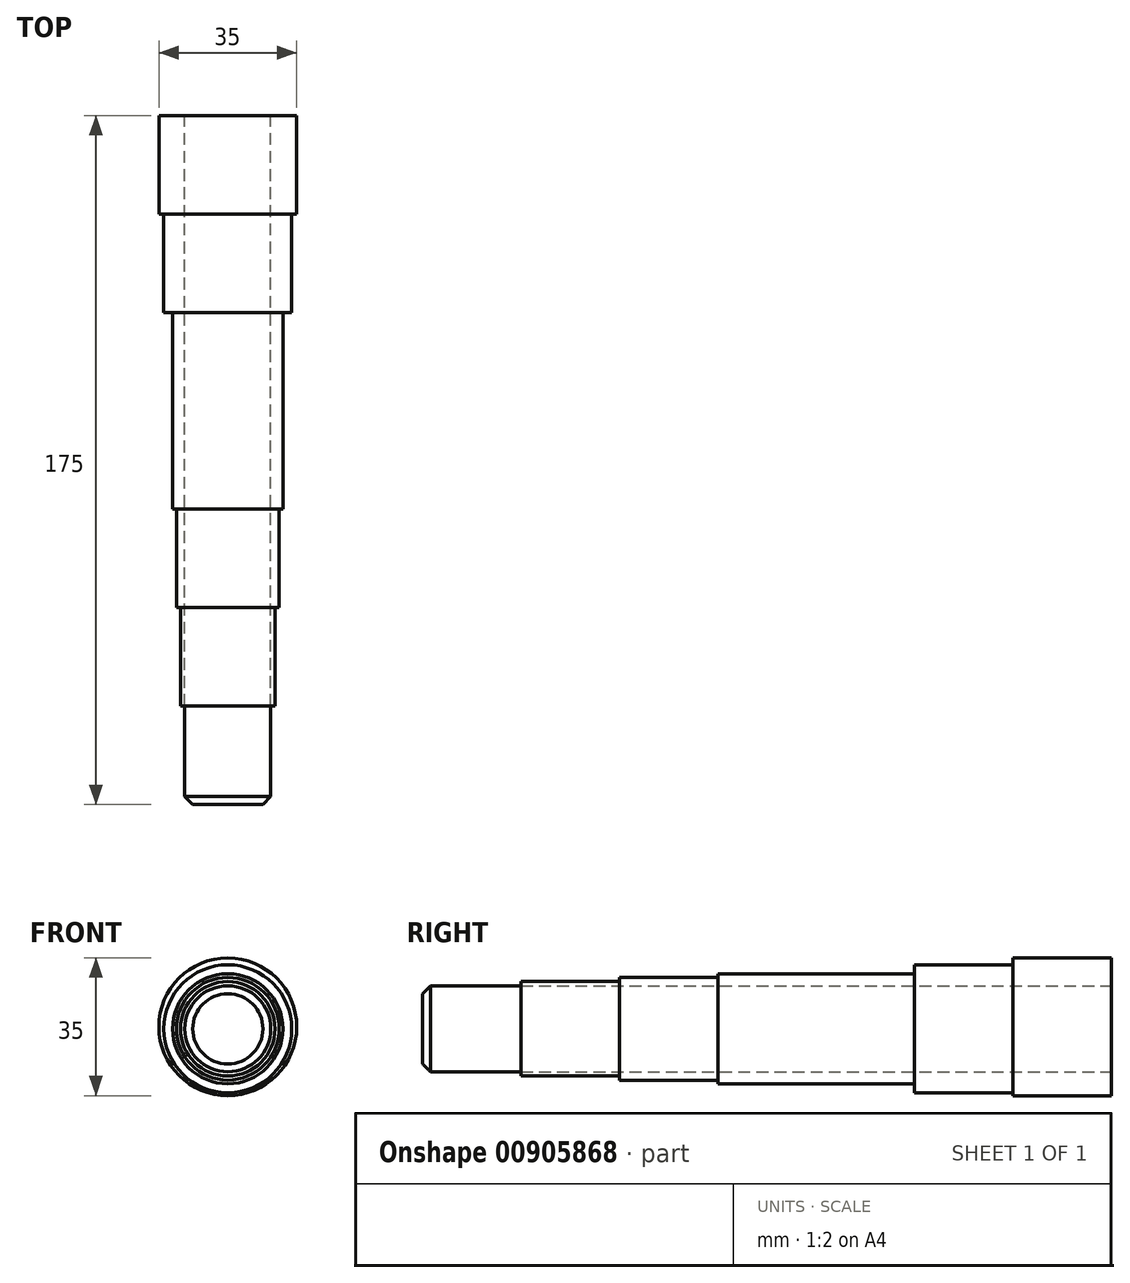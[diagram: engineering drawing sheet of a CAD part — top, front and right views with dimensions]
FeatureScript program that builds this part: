
annotation { "Feature Type Name" : "Feature", "Feature Type Description" : "" }
export const myFeature = defineFeature(function(context is Context, id is Id, definition is map)
    precondition{}
    {
        {
            var Q0;
            Q0=qCreatedBy(makeId("Front.planeOp"),FACE);
            var sketch = newSketch(context, id + "F0", { "sketchPlane" : qUnion([Q0])});
            skCircle(sketch, "E0", {"center": v(0, 0.51) * mm, "radius": 17.5 * mm});
            skSolve(sketch);
        }
        {
            var Q0;
            Q0=makeQuery(id+"F0.imprint","IMPRINT",FACE,{"disambiguationData":[TD([[makeQuery(id+"F0.imprint","IMPRINT",EDGE,{"derivedFrom":sQuery(id+"F0.wireOp",EDGE,"E0")}),1.0]])]});
            extrude(context, id + "F1", {"entities" : qUnion([Q0]), "depth" : 25 * mm, "offsetDistance" : 25 * mm});
        }
        {
            var Q0;
            Q0=qCreatedBy(makeId("Front.planeOp"),FACE);
            var sketch = newSketch(context, id + "F2", { "sketchPlane" : qUnion([Q0])});
            skCircle(sketch, "E1", {"center": v(0, 0) * mm, "radius": 16.25 * mm});
            skSolve(sketch);
        }
        {
            var Q0;
            Q0 = qSketchRegion(id + "F2", true);
            extrude(context, id + "F3", {"entities" : qUnion([Q0]), "depth" : 50 * mm, "offsetDistance" : 25 * mm});
        }
        {
            var Q0;
            Q0=qCreatedBy(makeId("Front.planeOp"),FACE);
            var sketch = newSketch(context, id + "F4", { "sketchPlane" : qUnion([Q0])});
            skCircle(sketch, "E2", {"center": v(0, 0) * mm, "radius": 14 * mm});
            skSolve(sketch);
        }
        {
            var Q0;
            Q0 = qSketchRegion(id + "F4", true);
            extrude(context, id + "F5", {"entities" : qUnion([Q0]), "operationType" : NewBodyOperationType.ADD, "depth" : 100 * mm, "offsetDistance" : 25 * mm});
        }
        {
            var Q0;
            Q0=qCreatedBy(makeId("Front.planeOp"),FACE);
            var sketch = newSketch(context, id + "F6", { "sketchPlane" : qUnion([Q0])});
            skCircle(sketch, "E3", {"center": v(0, 0) * mm, "radius": 13.05 * mm});
            skSolve(sketch);
        }
        {
            var Q0;
            Q0 = qSketchRegion(id + "F6", true);
            extrude(context, id + "F7", {"entities" : qUnion([Q0]), "operationType" : NewBodyOperationType.ADD, "depth" : 125 * mm, "offsetDistance" : 25 * mm});
        }
        {
            var Q0;
            Q0=qCreatedBy(makeId("Front.planeOp"),FACE);
            var sketch = newSketch(context, id + "F8", { "sketchPlane" : qUnion([Q0])});
            skCircle(sketch, "E4", {"center": v(0, 0) * mm, "radius": 12 * mm});
            skSolve(sketch);
        }
        {
            var Q0;
            Q0 = qSketchRegion(id + "F8", true);
            extrude(context, id + "F9", {"entities" : qUnion([Q0]), "operationType" : NewBodyOperationType.ADD, "depth" : 150 * mm, "offsetDistance" : 25 * mm});
        }
        {
            var Q0;
            Q0=qCreatedBy(makeId("Front.planeOp"),FACE);
            var sketch = newSketch(context, id + "F10", { "sketchPlane" : qUnion([Q0])});
            skCircle(sketch, "E5", {"center": v(0, 0) * mm, "radius": 10.93 * mm});
            skSolve(sketch);
        }
        {
            var Q0;
            Q0 = qSketchRegion(id + "F10", true);
            extrude(context, id + "F11", {"entities" : qUnion([Q0]), "depth" : 175 * mm, "offsetDistance" : 25 * mm});
        }
        {
            var Q0;
            Q0=makeQuery(id+"F11.opExtrude","CAP_FACE",FACE,{"disambiguationData":[OSD([sQuery(id+"F10.wireOp",EDGE,"E5")])],"isStart":false});
            chamfer(context, id + "F12", {"entities" : qUnion([Q0]), "width" : 2 * mm, "tangentPropagation" : true});
        }
    });
